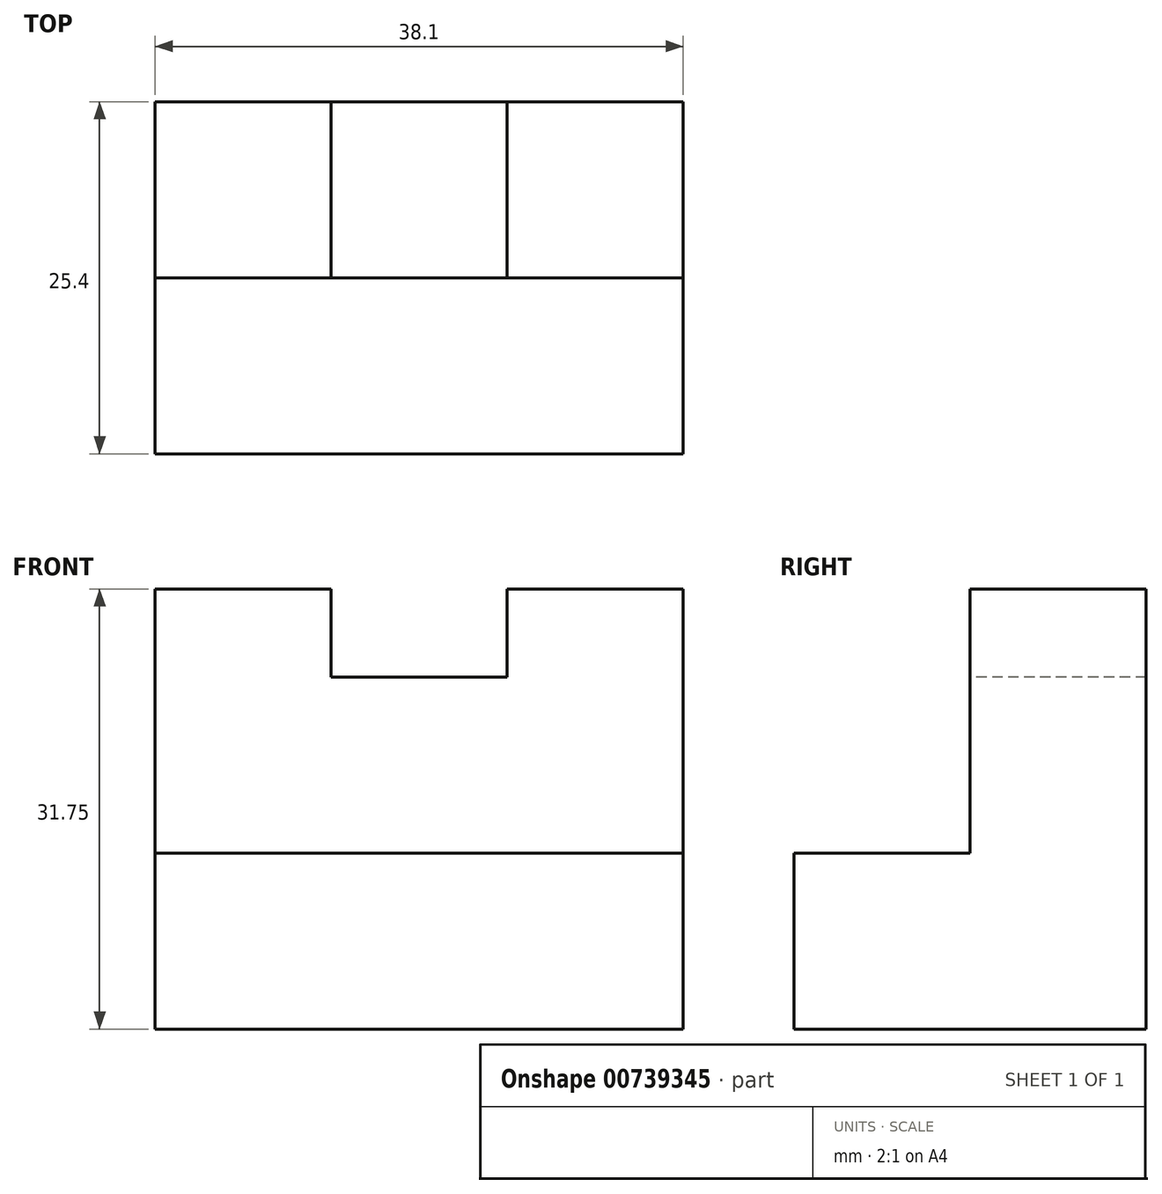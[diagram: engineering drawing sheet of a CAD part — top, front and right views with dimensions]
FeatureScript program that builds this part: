
annotation { "Feature Type Name" : "Feature", "Feature Type Description" : "" }
export const myFeature = defineFeature(function(context is Context, id is Id, definition is map)
    precondition{}
    {
        {
            var Q0;
            Q0=qCreatedBy(makeId("Front.planeOp"),FACE);
            var sketch = newSketch(context, id + "F0", { "sketchPlane" : qUnion([Q0])});
            skLineSegment(sketch, "E0", {"start": v(0, 0) * mm, "end": v(38.1, 0) * mm});
            skLineSegment(sketch, "E1", {"start": v(38.1, 0) * mm, "end": v(38.1, 31.75) * mm});
            skLineSegment(sketch, "E2", {"start": v(38.1, 31.75) * mm, "end": v(0, 31.75) * mm});
            skLineSegment(sketch, "E3", {"start": v(0, 31.75) * mm, "end": v(0, 0) * mm});
            skSolve(sketch);
        }
        {
            var Q0;
            Q0=makeQuery(id+"F0.imprint","IMPRINT",FACE,{"disambiguationData":[TD([[makeQuery(id+"F0.imprint","IMPRINT",EDGE,{"derivedFrom":sQuery(id+"F0.wireOp",EDGE,"E0")}),1.0]])]});
            extrude(context, id + "F1", {"entities" : qUnion([Q0]), "depth" : 25.4 * mm, "offsetDistance" : 25.4 * mm});
        }
        {
            var Q0;
            Q0=makeQuery(id+"F1.opExtrude","SWEPT_FACE",FACE,{"disambiguationData":[OSD([sQuery(id+"F0.wireOp",EDGE,"E1")])]});
            var sketch = newSketch(context, id + "F2", { "sketchPlane" : qUnion([Q0])});
            skLineSegment(sketch, "E4.bottom", {"start": v(-25.4, 31.75) * mm, "end": v(-12.7, 31.75) * mm});
            skLineSegment(sketch, "E4.top", {"start": v(-25.4, 12.7) * mm, "end": v(-12.7, 12.7) * mm});
            skLineSegment(sketch, "E4.left", {"start": v(-25.4, 31.75) * mm, "end": v(-25.4, 12.7) * mm});
            skLineSegment(sketch, "E4.right", {"start": v(-12.7, 31.75) * mm, "end": v(-12.7, 12.7) * mm});
            skSolve(sketch);
        }
        {
            var Q0;
            Q0=makeQuery(id+"F2.imprint","IMPRINT",FACE,{"disambiguationData":[TD([[makeQuery(id+"F2.imprint","IMPRINT",EDGE,{"derivedFrom":sQuery(id+"F2.wireOp",EDGE,"E4.bottom")}),-1.0]])]});
            extrude(context, id + "F3", {"entities" : qUnion([Q0]), "operationType" : NewBodyOperationType.REMOVE, "oppositeDirection" : true, "depth" : 38.1 * mm, "offsetDistance" : 25.4 * mm});
        }
        {
            var Q0;
            Q0=makeQuery(id+"F3.boolean.opBoolean","COPY",FACE,{"derivedFrom":makeQuery(id+"F3.opExtrude","SWEPT_FACE",FACE,{"disambiguationData":[OSD([sQuery(id+"F2.wireOp",EDGE,"E4.right")])]})});
            var sketch = newSketch(context, id + "F4", { "sketchPlane" : qUnion([Q0])});
            skLineSegment(sketch, "E5.bottom", {"start": v(12.7, 31.75) * mm, "end": v(25.4, 31.75) * mm});
            skLineSegment(sketch, "E5.top", {"start": v(12.7, 25.4) * mm, "end": v(25.4, 25.4) * mm});
            skLineSegment(sketch, "E5.left", {"start": v(12.7, 31.75) * mm, "end": v(12.7, 25.4) * mm});
            skLineSegment(sketch, "E5.right", {"start": v(25.4, 31.75) * mm, "end": v(25.4, 25.4) * mm});
            skSolve(sketch);
        }
        {
            var Q0;
            Q0=makeQuery(id+"F4.imprint","IMPRINT",FACE,{"disambiguationData":[TD([[makeQuery(id+"F4.imprint","IMPRINT",EDGE,{"derivedFrom":sQuery(id+"F4.wireOp",EDGE,"E5.bottom")}),-1.0]])]});
            extrude(context, id + "F5", {"entities" : qUnion([Q0]), "operationType" : NewBodyOperationType.REMOVE, "oppositeDirection" : true, "depth" : 12.7 * mm, "offsetDistance" : 25.4 * mm});
        }
    });
